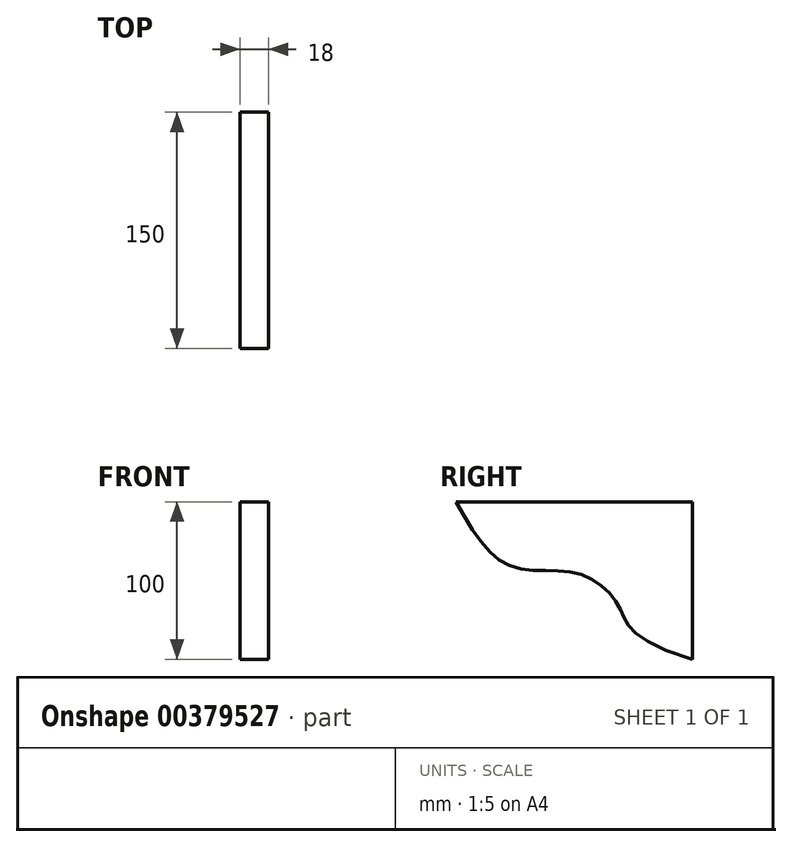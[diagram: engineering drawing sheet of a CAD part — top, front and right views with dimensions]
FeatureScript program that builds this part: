
annotation { "Feature Type Name" : "Feature", "Feature Type Description" : "" }
export const myFeature = defineFeature(function(context is Context, id is Id, definition is map)
    precondition{}
    {
        {
            var Q0;
            Q0=qCreatedBy(makeId("Right.planeOp"),FACE);
            var sketch = newSketch(context, id + "F0", { "sketchPlane" : qUnion([Q0])});
            skLineSegment(sketch, "E0", {"start": v(-71.3, 65.3) * mm, "end": v(78.7, 65.3) * mm});
            skLineSegment(sketch, "E1", {"start": v(78.7, 65.3) * mm, "end": v(78.7, -34.7) * mm});
            skFitSpline(sketch, "E2", {"points": [v(-71.3, 65.3) * mm, v(-35.89, 24.33) * mm, v(6.73, 19.6) * mm, v(31.78, -0.66) * mm, v(78.7, -34.7) * mm], "startDerivative": vector(120.51, -222.34) * mm, "endDerivative": vector(454.24, -137.32) * mm});
            skSolve(sketch);
        }
        {
            var Q0;
            Q0=makeQuery(id+"F0.imprint","IMPRINT",FACE,{"disambiguationData":[TD([[makeQuery(id+"F0.imprint","IMPRINT",EDGE,{"derivedFrom":sQuery(id+"F0.wireOp",EDGE,"E0")}),-1.0]])]});
            extrude(context, id + "F1", {"entities" : qUnion([Q0]), "depth" : 18 * mm});
        }
    });
